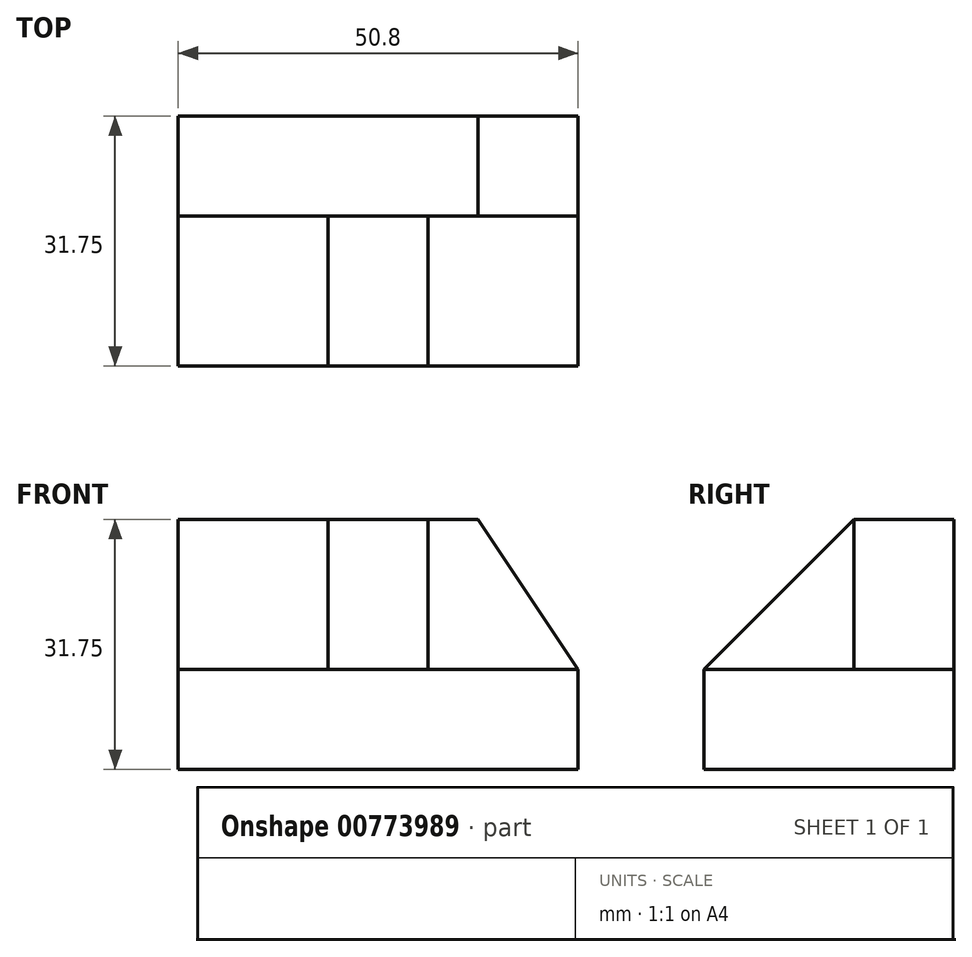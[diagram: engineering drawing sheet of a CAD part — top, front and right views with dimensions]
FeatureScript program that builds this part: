
annotation { "Feature Type Name" : "Feature", "Feature Type Description" : "" }
export const myFeature = defineFeature(function(context is Context, id is Id, definition is map)
    precondition{}
    {
        {
            var Q0;
            Q0=qCreatedBy(makeId("Front.planeOp"),FACE);
            var sketch = newSketch(context, id + "F0", { "sketchPlane" : qUnion([Q0])});
            skLineSegment(sketch, "E0", {"start": v(0, 0) * mm, "end": v(50.8, 0) * mm});
            skLineSegment(sketch, "E1", {"start": v(50.8, 0) * mm, "end": v(50.8, 31.75) * mm});
            skLineSegment(sketch, "E2", {"start": v(50.8, 31.75) * mm, "end": v(0, 31.75) * mm});
            skLineSegment(sketch, "E3", {"start": v(0, 31.75) * mm, "end": v(0, 0) * mm});
            skSolve(sketch);
        }
        {
            var Q0;
            Q0=makeQuery(id+"F0.imprint","IMPRINT",FACE,{"disambiguationData":[TD([[makeQuery(id+"F0.imprint","IMPRINT",EDGE,{"derivedFrom":sQuery(id+"F0.wireOp",EDGE,"E0")}),1.0]])]});
            extrude(context, id + "F1", {"entities" : qUnion([Q0]), "depth" : 31.75 * mm, "offsetDistance" : 25.4 * mm});
        }
        {
            var Q0;
            Q0=makeQuery(id+"F1.opExtrude","CAP_FACE",FACE,{"disambiguationData":[OSD([sQuery(id+"F0.wireOp",EDGE,"E0"),sQuery(id+"F0.wireOp",EDGE,"E1"),sQuery(id+"F0.wireOp",EDGE,"E2"),sQuery(id+"F0.wireOp",EDGE,"E3")])],"isStart":false});
            var sketch = newSketch(context, id + "F2", { "sketchPlane" : qUnion([Q0])});
            skLineSegment(sketch, "E4", {"start": v(50.8, 0) * mm, "end": v(50.8, 12.7) * mm});
            skLineSegment(sketch, "E5", {"start": v(0, 0) * mm, "end": v(0, 12.7) * mm});
            skLineSegment(sketch, "E6", {"start": v(0, 12.7) * mm, "end": v(50.8, 12.7) * mm});
            skLineSegment(sketch, "E7", {"start": v(50.8, 31.75) * mm, "end": v(31.75, 31.75) * mm});
            skLineSegment(sketch, "E8", {"start": v(0, 31.75) * mm, "end": v(19.05, 31.75) * mm});
            skLineSegment(sketch, "E9", {"start": v(31.75, 31.75) * mm, "end": v(31.75, 12.7) * mm});
            skLineSegment(sketch, "E10", {"start": v(19.05, 31.75) * mm, "end": v(19.05, 12.7) * mm});
            skSolve(sketch);
        }
        {
            var Q0;
            {var subQ4=sQuery(id+"F2.wireOp",EDGE,"E8");Q0=makeQuery(id+"F2.imprint","IMPRINT",FACE,{"disambiguationData":[TD([[makeQuery(id+"F2.imprint","IMPRINT",EDGE,{"derivedFrom":subQ4}),1.0]])]});}
            var Q1;
            {var subQ4=sQuery(id+"F2.wireOp",EDGE,"E7");Q1=makeQuery(id+"F2.imprint","IMPRINT",FACE,{"disambiguationData":[TD([[makeQuery(id+"F2.imprint","IMPRINT",EDGE,{"derivedFrom":subQ4}),1.0]])]});}
            extrude(context, id + "F3", {"entities" : qUnion([Q0, Q1]), "operationType" : NewBodyOperationType.REMOVE, "oppositeDirection" : true, "depth" : 19.05 * mm, "offsetDistance" : 25.4 * mm});
        }
        {
            var Q0;
            Q0=makeQuery(id+"F3.boolean.opBoolean","COPY",FACE,{"derivedFrom":makeQuery(id+"F3.opExtrude","SWEPT_FACE",FACE,{"disambiguationData":[OSD([sQuery(id+"F2.wireOp",EDGE,"E9")])]})});
            var sketch = newSketch(context, id + "F4", { "sketchPlane" : qUnion([Q0])});
            skLineSegment(sketch, "E11", {"start": v(-12.7, 31.75) * mm, "end": v(-31.75, 12.7) * mm});
            skSolve(sketch);
        }
        {
            var Q0;
            Q0=makeQuery(id+"F4.imprint","IMPRINT",FACE,{"disambiguationData":[TD([[makeQuery(id+"F4.imprint","IMPRINT",EDGE,{"derivedFrom":sQuery(id+"F4.wireOp",EDGE,"E11")}),-1.0]])]});
            extrude(context, id + "F5", {"entities" : qUnion([Q0]), "operationType" : NewBodyOperationType.REMOVE, "oppositeDirection" : true, "depth" : 25.4 * mm, "offsetDistance" : 25.4 * mm});
        }
        {
            var Q0;
            Q0=makeQuery(id+"F3.boolean.opBoolean","COPY",FACE,{"derivedFrom":makeQuery(id+"F3.opExtrude","CAP_FACE",FACE,{"disambiguationData":[OSD([sQuery(id+"F0.wireOp",EDGE,"E1"),sQuery(id+"F2.wireOp",EDGE,"E6"),sQuery(id+"F2.wireOp",EDGE,"E7"),sQuery(id+"F2.wireOp",EDGE,"E9")])],"isStart":false})});
            var sketch = newSketch(context, id + "F6", { "sketchPlane" : qUnion([Q0])});
            skLineSegment(sketch, "E12", {"start": v(31.75, 31.75) * mm, "end": v(38.1, 31.75) * mm});
            skLineSegment(sketch, "E13", {"start": v(38.1, 31.75) * mm, "end": v(50.8, 12.7) * mm});
            skSolve(sketch);
        }
        {
            var Q0;
            {var subQ0=sQuery(id+"F6.wireOp",EDGE,"E13");Q0=makeQuery(id+"F6.imprint","IMPRINT",FACE,{"disambiguationData":[TD([[makeQuery(id+"F6.imprint","IMPRINT",EDGE,{"derivedFrom":subQ0}),1.0]])]});}
            extrude(context, id + "F7", {"entities" : qUnion([Q0]), "operationType" : NewBodyOperationType.REMOVE, "oppositeDirection" : true, "depth" : 25.4 * mm, "offsetDistance" : 25.4 * mm});
        }
    });
